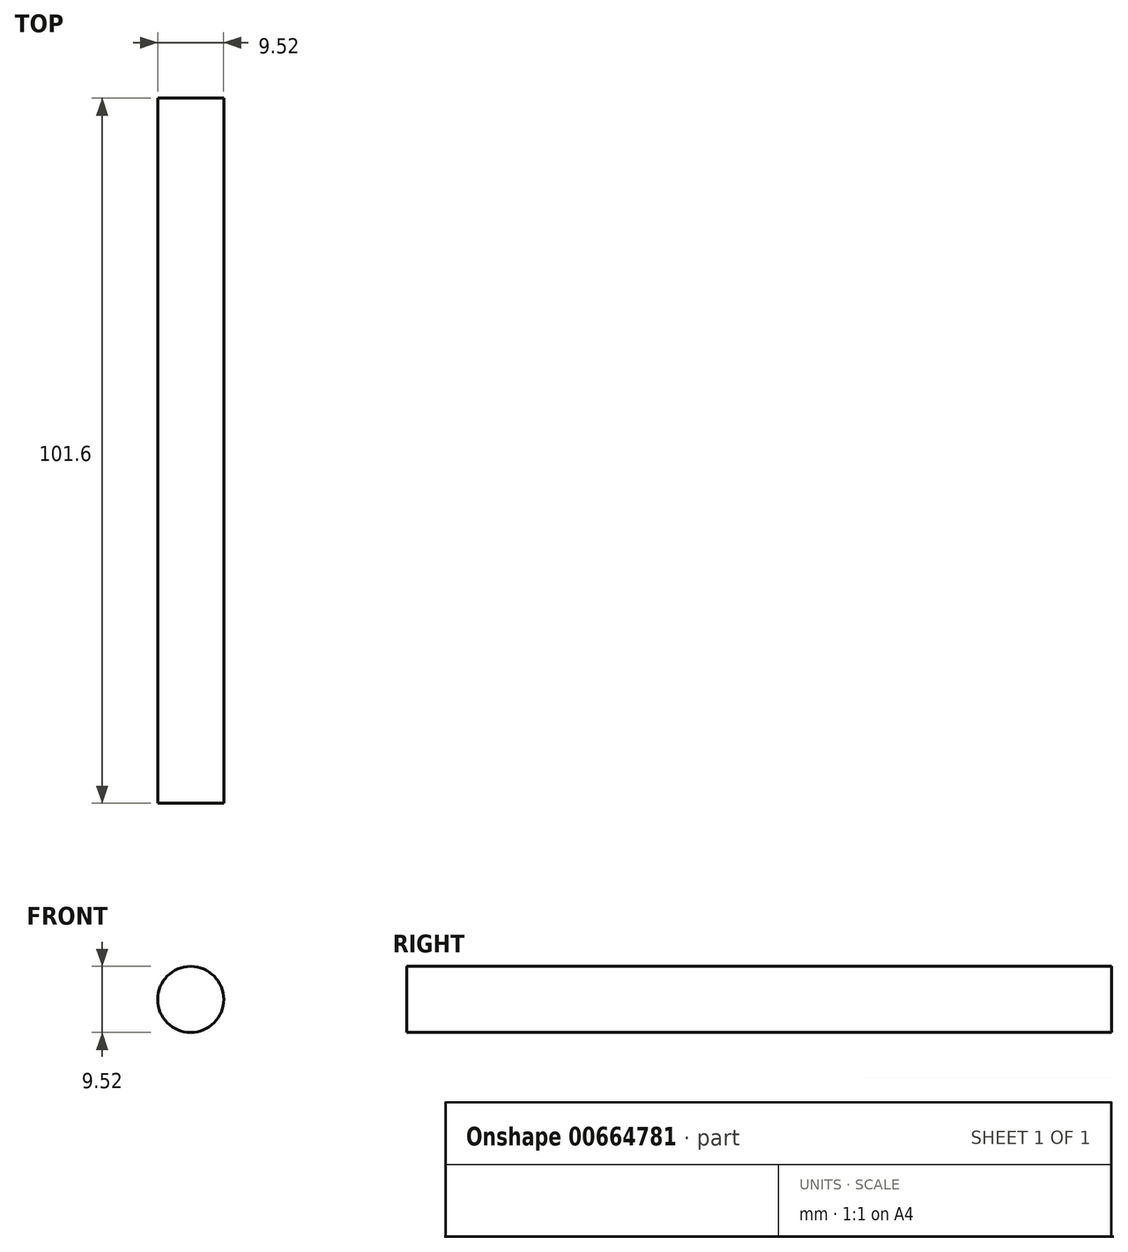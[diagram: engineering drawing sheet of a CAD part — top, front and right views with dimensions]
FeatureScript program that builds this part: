
annotation { "Feature Type Name" : "Feature", "Feature Type Description" : "" }
export const myFeature = defineFeature(function(context is Context, id is Id, definition is map)
    precondition{}
    {
        {
            var Q0;
            Q0=qCreatedBy(makeId("Front.planeOp"),FACE);
            var sketch = newSketch(context, id + "F0", { "sketchPlane" : qUnion([Q0])});
            skCircle(sketch, "E0", {"center": v(0, 0) * mm, "radius": 4.76 * mm});
            skSolve(sketch);
        }
        {
            var Q0;
            Q0 = qSketchRegion(id + "F0", true);
            extrude(context, id + "F1", {"entities" : qUnion([Q0]), "depth" : 101.6 * mm, "offsetDistance" : 25.4 * mm});
        }
    });
